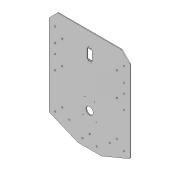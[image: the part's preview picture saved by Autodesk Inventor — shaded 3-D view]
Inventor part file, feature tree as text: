
AUTODESK INVENTOR PART (.ipt)
format: ipt  version: 2020 (Build 240168000, 168)  size: 361,472 bytes
history: native  units: mm
features: sketch x4, other x3, extrude x3, projected_geometry x1
ambient origin geometry x8: Origin, YZ Plane, XZ Plane, XY Plane, X Axis, Y Axis, Z Axis, Center Point
bodies: Body1 (feature_tree)
feature tree (11):
  other  "솔리드1"
  extrude  "돌출2"  Depth=3.0mm
  other  "모서리 라운드1"
  extrude  "돌출3"  Depth=140.0mm
  extrude  "돌출4"  Depth=27.87mm
  sketch  "스케치1"
  sketch  "스케치3"
  sketch  "스케치4"
  sketch  "스케치5"
  projected_geometry  "투영된 루프1"
  other  "정의1"
